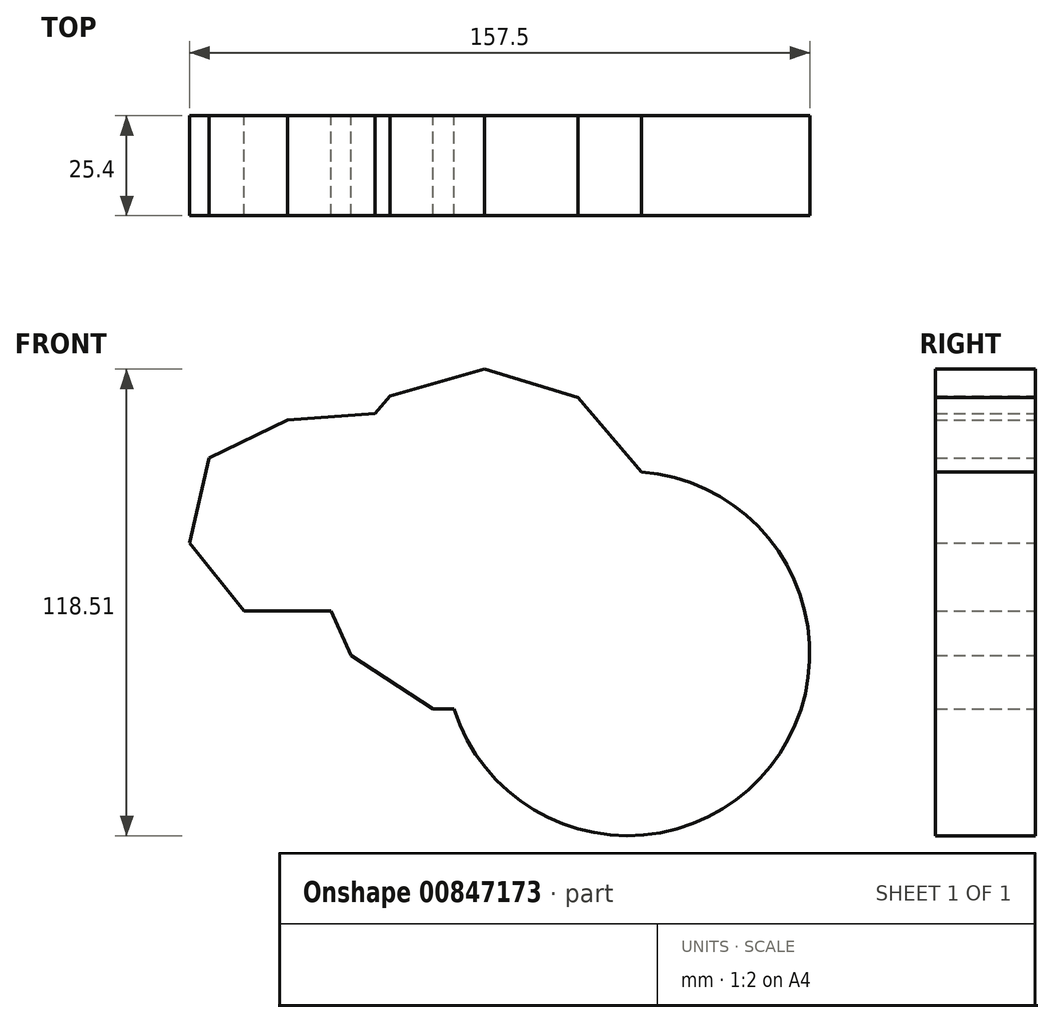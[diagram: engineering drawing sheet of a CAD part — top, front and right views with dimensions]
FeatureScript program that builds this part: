
annotation { "Feature Type Name" : "Feature", "Feature Type Description" : "" }
export const myFeature = defineFeature(function(context is Context, id is Id, definition is map)
    precondition{}
    {
        {
            var Q0;
            Q0=qCreatedBy(makeId("Front.planeOp"),FACE);
            var sketch = newSketch(context, id + "F0", { "sketchPlane" : qUnion([Q0])});
            skCircle(sketch, "E0.cCircle", {"center": v(-49.66, 40.98) * mm, "radius": 22.94 * mm, "construction": true});
            skLineSegment(sketch, "E0.0", {"start": v(-38.6, 18.04) * mm, "end": v(-60.7, 18.04) * mm});
            skLineSegment(sketch, "E0.1", {"start": v(-60.7, 18.04) * mm, "end": v(-74.48, 35.32) * mm});
            skLineSegment(sketch, "E0.2", {"start": v(-74.48, 35.32) * mm, "end": v(-69.56, 56.86) * mm});
            skLineSegment(sketch, "E0.3", {"start": v(-69.56, 56.86) * mm, "end": v(-49.66, 66.45) * mm});
            skLineSegment(sketch, "E0.4", {"start": v(-49.66, 66.45) * mm, "end": v(-29.75, 56.86) * mm});
            skLineSegment(sketch, "E0.5", {"start": v(-29.75, 56.86) * mm, "end": v(-24.83, 35.32) * mm});
            skLineSegment(sketch, "E0.6", {"start": v(-24.83, 35.32) * mm, "end": v(-38.6, 18.04) * mm});
            skPoint(sketch, "E0.0.midPoint", {"position": v(-49.66, 18.04) * mm});
            skCircle(sketch, "E1.cCircle", {"center": v(0, 35.32) * mm, "radius": 42.3 * mm, "construction": true});
            skLineSegment(sketch, "E1.0", {"start": v(-33.54, 6.7) * mm, "end": v(-43.68, 29.38) * mm});
            skLineSegment(sketch, "E1.1", {"start": v(-43.68, 29.38) * mm, "end": v(-39.96, 53.94) * mm});
            skLineSegment(sketch, "E1.2", {"start": v(-39.96, 53.94) * mm, "end": v(-23.55, 72.59) * mm});
            skLineSegment(sketch, "E1.3", {"start": v(-23.55, 72.59) * mm, "end": v(0.34, 79.4) * mm});
            skLineSegment(sketch, "E1.4", {"start": v(0.34, 79.4) * mm, "end": v(24.12, 72.22) * mm});
            skLineSegment(sketch, "E1.5", {"start": v(24.12, 72.22) * mm, "end": v(40.24, 53.32) * mm});
            skLineSegment(sketch, "E1.6", {"start": v(40.24, 53.32) * mm, "end": v(43.58, 28.7) * mm});
            skLineSegment(sketch, "E1.7", {"start": v(43.58, 28.7) * mm, "end": v(33.1, 6.2) * mm});
            skLineSegment(sketch, "E1.8", {"start": v(33.1, 6.2) * mm, "end": v(12.1, -7.07) * mm});
            skLineSegment(sketch, "E1.9", {"start": v(12.1, -7.07) * mm, "end": v(-12.74, -6.88) * mm});
            skLineSegment(sketch, "E1.10", {"start": v(-12.74, -6.88) * mm, "end": v(-33.54, 6.7) * mm});
            skPoint(sketch, "E1.0.midPoint", {"position": v(-38.6, 18.04) * mm});
            skArc(sketch, "E2", {"start": v(0, 35.32) * mm, "mid": v(55.64, -35.07) * mm, "end": v(40.24, 53.32) * mm});
            skLineSegment(sketch, "E3", {"start": v(-49.66, 66.45) * mm, "end": v(-49.66, 40.98) * mm});
            skLineSegment(sketch, "E4", {"start": v(-49.66, 40.98) * mm, "end": v(-38.6, 18.04) * mm});
            skLineSegment(sketch, "E5", {"start": v(-38.6, 18.04) * mm, "end": v(0, 35.32) * mm});
            skLineSegment(sketch, "E6", {"start": v(0, 35.32) * mm, "end": v(12.1, -7.07) * mm});
            skLineSegment(sketch, "E7", {"start": v(12.1, -7.07) * mm, "end": v(36.74, 7.17) * mm});
            skLineSegment(sketch, "E8", {"start": v(36.74, 7.17) * mm, "end": v(24.12, 72.22) * mm});
            skLineSegment(sketch, "E9", {"start": v(24.12, 72.22) * mm, "end": v(-49.66, 66.45) * mm});
            skSolve(sketch);
        }
        {
            var Q0;
            Q0=makeQuery(id+"F0.imprint","IMPRINT",FACE,{"disambiguationData":[TD([[makeQuery(id+"F0.imprint","IMPRINT",EDGE,{"derivedFrom":sQuery(id+"F0.wireOp",EDGE,"E0.0")}),-1.0]])]});
            var Q1;
            {var subQ3=sQuery(id+"F0.wireOp",EDGE,"E0.5");Q1=makeQuery(id+"F0.imprint","IMPRINT",FACE,{"disambiguationData":[TD([[makeQuery(id+"F0.imprint","IMPRINT",EDGE,{"derivedFrom":subQ3}),-1.0]])]});}
            var Q2;
            {var subQ1=sQuery(id+"F0.wireOp",EDGE,"E1.1");Q2=makeQuery(id+"F0.imprint","IMPRINT",FACE,{"disambiguationData":[TD([[makeQuery(id+"F0.imprint","IMPRINT",EDGE,{"derivedFrom":subQ1}),1.0]])]});}
            var Q3;
            {var subQ0=sQuery(id+"F0.wireOp",EDGE,"E9");var subQ3=sQuery(id+"F0.wireOp",EDGE,"E1.2");var subQ5=makeQuery(id+"F0.imprint","INTERSECT",VERTEX,{"derivedFrom":[subQ3,subQ0]});Q3=makeQuery(id+"F0.imprint","IMPRINT",FACE,{"disambiguationData":[TD([[makeQuery(id+"F0.imprint","IMPRINT",EDGE,{"disambiguationData":[TD([[subQ5,1.0]])],"derivedFrom":subQ3}),1.0]])]});}
            var Q4;
            {var subQ5=sQuery(id+"F0.wireOp",EDGE,"E0.5");Q4=makeQuery(id+"F0.imprint","IMPRINT",FACE,{"disambiguationData":[TD([[makeQuery(id+"F0.imprint","IMPRINT",EDGE,{"derivedFrom":subQ5}),1.0]])]});}
            var Q5;
            {var subQ0=sQuery(id+"F0.wireOp",EDGE,"E1.3");Q5=makeQuery(id+"F0.imprint","IMPRINT",FACE,{"disambiguationData":[TD([[makeQuery(id+"F0.imprint","IMPRINT",EDGE,{"derivedFrom":subQ0}),-1.0]])]});}
            var Q6;
            {var subQ4=sQuery(id+"F0.wireOp",EDGE,"E1.10");Q6=makeQuery(id+"F0.imprint","IMPRINT",FACE,{"disambiguationData":[TD([[makeQuery(id+"F0.imprint","IMPRINT",EDGE,{"derivedFrom":subQ4}),-1.0]])]});}
            var Q7;
            {var subQ0=sQuery(id+"F0.wireOp",EDGE,"E6");Q7=makeQuery(id+"F0.imprint","IMPRINT",FACE,{"disambiguationData":[TD([[makeQuery(id+"F0.imprint","IMPRINT",EDGE,{"derivedFrom":subQ0}),-1.0]])]});}
            var Q8;
            {var subQ0=sQuery(id+"F0.wireOp",EDGE,"E1.5");Q8=makeQuery(id+"F0.imprint","IMPRINT",FACE,{"disambiguationData":[TD([[makeQuery(id+"F0.imprint","IMPRINT",EDGE,{"derivedFrom":subQ0}),-1.0]])]});}
            var Q9;
            {var subQ1=sQuery(id+"F0.wireOp",EDGE,"E1.6");Q9=makeQuery(id+"F0.imprint","IMPRINT",FACE,{"disambiguationData":[TD([[makeQuery(id+"F0.imprint","IMPRINT",EDGE,{"derivedFrom":subQ1}),1.0]])]});}
            var Q10;
            {var subQ0=sQuery(id+"F0.wireOp",EDGE,"E1.8");Q10=makeQuery(id+"F0.imprint","IMPRINT",FACE,{"disambiguationData":[TD([[makeQuery(id+"F0.imprint","IMPRINT",EDGE,{"derivedFrom":subQ0}),1.0]])]});}
            extrude(context, id + "F1", {"entities" : qUnion([Q0, Q1, Q2, Q3, Q4, Q5, Q6, Q7, Q8, Q9, Q10]), "depth" : 25.4 * mm, "offsetDistance" : 25.4 * mm});
        }
    });
